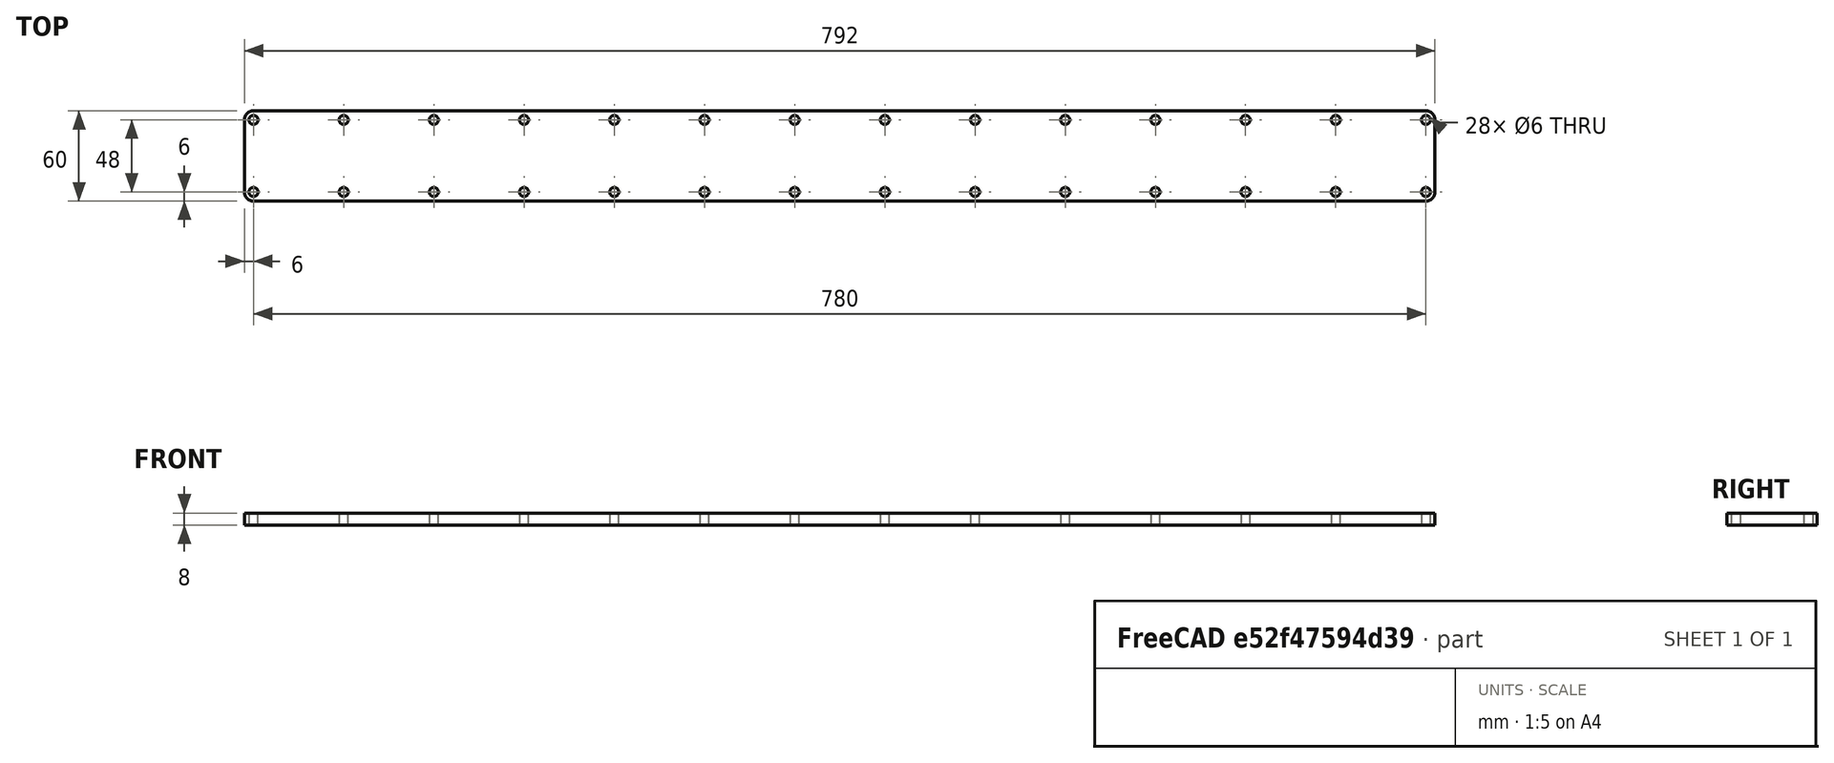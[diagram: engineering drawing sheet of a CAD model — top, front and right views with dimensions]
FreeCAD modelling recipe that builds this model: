
FCSTD DOCUMENT  (FreeCAD 0.19R24366 (Git))
Label: Tapped plate for slider rail mounting
License: All rights reserved
LicenseURL: http://en.wikipedia.org/wiki/All_rights_reserved
objects: Sketcher::SketchObject×1, PartDesign::Pad×1, PartDesign::Body×1
note: 4 computed .brp shape members not serialized (recipe doc carries the construction recipe); baked Part::Feature solids carry a one-line shape summary decoded from their .brp

FEATURE [Sketcher::SketchObject] Sketch  label="Plate sketch"
  FullyConstrained = true
  MapMode = 5
  Support = -> [XY_Plane]
  sketch-geometry (121):
    g0: LineSegment StartX=0 StartY=-1e-16 StartZ=0 EndX=0 EndY=24 EndZ=0
    g1: LineSegment StartX=0 StartY=-1e-16 StartZ=0 EndX=0 EndY=-24 EndZ=0
    g2: LineSegment StartX=0 StartY=24 StartZ=0 EndX=6 EndY=24 EndZ=0
    g3: LineSegment StartX=0 StartY=-24 StartZ=0 EndX=6 EndY=-24 EndZ=0
    g4: Circle CenterX=6 CenterY=-24 CenterZ=0 NormalX=0 NormalY=0 NormalZ=1 AngleXU=0 Radius=3
    g5: Circle CenterX=6 CenterY=24 CenterZ=0 NormalX=0 NormalY=0 NormalZ=1 AngleXU=0 Radius=3
    g6: ArcOfCircle CenterX=6 CenterY=24 CenterZ=0 NormalX=0 NormalY=0 NormalZ=1 AngleXU=0 Radius=6 StartAngle=1.5708 EndAngle=3.14159
    g7: ArcOfCircle CenterX=6 CenterY=-24 CenterZ=0 NormalX=0 NormalY=0 NormalZ=1 AngleXU=0 Radius=6 StartAngle=3.14159 EndAngle=4.71239
    g8: LineSegment StartX=786 StartY=-30 StartZ=0 EndX=6 EndY=-30 EndZ=0
    g9: LineSegment StartX=6 StartY=30 StartZ=0 EndX=786 EndY=30 EndZ=0
    g10: Circle CenterX=66 CenterY=24 CenterZ=0 NormalX=0 NormalY=0 NormalZ=1 AngleXU=0 Radius=3
    g11: LineSegment StartX=6 StartY=24 StartZ=0 EndX=66 EndY=24 EndZ=0
    g12: Circle CenterX=126 CenterY=24 CenterZ=0 NormalX=0 NormalY=0 NormalZ=1 AngleXU=0 Radius=3
    g13: LineSegment StartX=66 StartY=24 StartZ=0 EndX=126 EndY=24 EndZ=0
    g14: Circle CenterX=186 CenterY=24 CenterZ=0 NormalX=0 NormalY=0 NormalZ=1 AngleXU=0 Radius=3
    g15: LineSegment StartX=126 StartY=24 StartZ=0 EndX=186 EndY=24 EndZ=0
    g16: Circle CenterX=246 CenterY=24 CenterZ=0 NormalX=0 NormalY=0 NormalZ=1 AngleXU=0 Radius=3
    g17: LineSegment StartX=186 StartY=24 StartZ=0 EndX=246 EndY=24 EndZ=0
    g18: Circle CenterX=306 CenterY=24 CenterZ=0 NormalX=0 NormalY=0 NormalZ=1 AngleXU=0 Radius=3
    g19: LineSegment StartX=246 StartY=24 StartZ=0 EndX=306 EndY=24 EndZ=0
    g20: Circle CenterX=366 CenterY=24 CenterZ=0 NormalX=0 NormalY=0 NormalZ=1 AngleXU=0 Radius=3
    g21: LineSegment StartX=306 StartY=24 StartZ=0 EndX=366 EndY=24 EndZ=0
    g22: Circle CenterX=426 CenterY=24 CenterZ=0 NormalX=0 NormalY=0 NormalZ=1 AngleXU=0 Radius=3
    g23: LineSegment StartX=366 StartY=24 StartZ=0 EndX=426 EndY=24 EndZ=0
    g24: Circle CenterX=486 CenterY=24 CenterZ=0 NormalX=0 NormalY=0 NormalZ=1 AngleXU=0 Radius=3
    g25: LineSegment StartX=426 StartY=24 StartZ=0 EndX=486 EndY=24 EndZ=0
    g26: Circle CenterX=546 CenterY=24 CenterZ=0 NormalX=0 NormalY=0 NormalZ=1 AngleXU=0 Radius=3
    g27: LineSegment StartX=486 StartY=24 StartZ=0 EndX=546 EndY=24 EndZ=0
    g28: Circle CenterX=606 CenterY=24 CenterZ=0 NormalX=0 NormalY=0 NormalZ=1 AngleXU=0 Radius=3
    g29: LineSegment StartX=546 StartY=24 StartZ=0 EndX=606 EndY=24 EndZ=0
    g30: Circle CenterX=666 CenterY=24 CenterZ=0 NormalX=0 NormalY=0 NormalZ=1 AngleXU=0 Radius=3
    g31: LineSegment StartX=606 StartY=24 StartZ=0 EndX=666 EndY=24 EndZ=0
    g32: Circle CenterX=726 CenterY=24 CenterZ=0 NormalX=0 NormalY=0 NormalZ=1 AngleXU=0 Radius=3
    g33: LineSegment StartX=666 StartY=24 StartZ=0 EndX=726 EndY=24 EndZ=0
    g34: Circle CenterX=786 CenterY=24 CenterZ=0 NormalX=0 NormalY=0 NormalZ=1 AngleXU=0 Radius=3
    g35: LineSegment StartX=726 StartY=24 StartZ=0 EndX=786 EndY=24 EndZ=0
    g36: Circle CenterX=66 CenterY=-24 CenterZ=0 NormalX=0 NormalY=0 NormalZ=1 AngleXU=0 Radius=3
    g37: LineSegment StartX=6 StartY=-24 StartZ=0 EndX=66 EndY=-24 EndZ=0
    g38: Circle CenterX=126 CenterY=-24 CenterZ=0 NormalX=0 NormalY=0 NormalZ=1 AngleXU=0 Radius=3
    g39: LineSegment StartX=66 StartY=-24 StartZ=0 EndX=126 EndY=-24 EndZ=0
    g40: Circle CenterX=186 CenterY=-24 CenterZ=0 NormalX=0 NormalY=0 NormalZ=1 AngleXU=0 Radius=3
    g41: LineSegment StartX=126 StartY=-24 StartZ=0 EndX=186 EndY=-24 EndZ=0
    g42: Circle CenterX=246 CenterY=-24 CenterZ=0 NormalX=0 NormalY=0 NormalZ=1 AngleXU=0 Radius=3
    g43: LineSegment StartX=186 StartY=-24 StartZ=0 EndX=246 EndY=-24 EndZ=0
    g44: Circle CenterX=306 CenterY=-24 CenterZ=0 NormalX=0 NormalY=0 NormalZ=1 AngleXU=0 Radius=3
    g45: LineSegment StartX=246 StartY=-24 StartZ=0 EndX=306 EndY=-24 EndZ=0
    g46: Circle CenterX=366 CenterY=-24 CenterZ=0 NormalX=0 NormalY=0 NormalZ=1 AngleXU=0 Radius=3
    g47: LineSegment StartX=306 StartY=-24 StartZ=0 EndX=366 EndY=-24 EndZ=0
    g48: Circle CenterX=426 CenterY=-24 CenterZ=0 NormalX=0 NormalY=0 NormalZ=1 AngleXU=0 Radius=3
    g49: LineSegment StartX=366 StartY=-24 StartZ=0 EndX=426 EndY=-24 EndZ=0
    g50: Circle CenterX=486 CenterY=-24 CenterZ=0 NormalX=0 NormalY=0 NormalZ=1 AngleXU=0 Radius=3
    g51: LineSegment StartX=426 StartY=-24 StartZ=0 EndX=486 EndY=-24 EndZ=0
    g52: Circle CenterX=546 CenterY=-24 CenterZ=0 NormalX=0 NormalY=0 NormalZ=1 AngleXU=0 Radius=3
    g53: LineSegment StartX=486 StartY=-24 StartZ=0 EndX=546 EndY=-24 EndZ=0
    g54: Circle CenterX=606 CenterY=-24 CenterZ=0 NormalX=0 NormalY=0 NormalZ=1 AngleXU=0 Radius=3
    g55: LineSegment StartX=546 StartY=-24 StartZ=0 EndX=606 EndY=-24 EndZ=0
    g56: Circle CenterX=666 CenterY=-24 CenterZ=0 NormalX=0 NormalY=0 NormalZ=1 AngleXU=0 Radius=3
    g57: LineSegment StartX=606 StartY=-24 StartZ=0 EndX=666 EndY=-24 EndZ=0
    g58: Circle CenterX=726 CenterY=-24 CenterZ=0 NormalX=0 NormalY=0 NormalZ=1 AngleXU=0 Radius=3
    g59: LineSegment StartX=666 StartY=-24 StartZ=0 EndX=726 EndY=-24 EndZ=0
    g60: Circle CenterX=786 CenterY=-24 CenterZ=0 NormalX=0 NormalY=0 NormalZ=1 AngleXU=0 Radius=3
    g61: LineSegment StartX=726 StartY=-24 StartZ=0 EndX=786 EndY=-24 EndZ=0
    g62: ArcOfCircle CenterX=786 CenterY=-24 CenterZ=0 NormalX=0 NormalY=0 NormalZ=1 AngleXU=0 Radius=6 StartAngle=4.71239 EndAngle=6.28319
    g63: ArcOfCircle CenterX=786 CenterY=24 CenterZ=0 NormalX=0 NormalY=0 NormalZ=1 AngleXU=0 Radius=6 StartAngle=1.62478e-06 EndAngle=1.5708
    g64: LineSegment StartX=792 StartY=24 StartZ=0 EndX=792 EndY=-24 EndZ=0
    g65: LineSegment StartX=3 StartY=24 StartZ=0 EndX=9 EndY=24 EndZ=0
    g66: LineSegment StartX=6 StartY=27 StartZ=0 EndX=6 EndY=21 EndZ=0
    g67: LineSegment StartX=66 StartY=27 StartZ=0 EndX=66 EndY=21 EndZ=0
    g68: LineSegment StartX=63 StartY=24 StartZ=0 EndX=69 EndY=24 EndZ=0
    g69: LineSegment StartX=126 StartY=27 StartZ=0 EndX=126 EndY=21 EndZ=0
    g70: LineSegment StartX=123 StartY=24 StartZ=0 EndX=129 EndY=24 EndZ=0
    g71: LineSegment StartX=186 StartY=27 StartZ=0 EndX=186 EndY=21 EndZ=0
    g72: LineSegment StartX=183 StartY=24 StartZ=0 EndX=189 EndY=24 EndZ=0
    g73: LineSegment StartX=246 StartY=27 StartZ=0 EndX=246 EndY=21 EndZ=0
    g74: LineSegment StartX=243 StartY=24 StartZ=0 EndX=249 EndY=24 EndZ=0
    g75: LineSegment StartX=306 StartY=27 StartZ=0 EndX=306 EndY=21 EndZ=0
    g76: LineSegment StartX=303 StartY=24 StartZ=0 EndX=309 EndY=24 EndZ=0
    g77: LineSegment StartX=366 StartY=27 StartZ=0 EndX=366 EndY=21 EndZ=0
    g78: LineSegment StartX=363 StartY=24 StartZ=0 EndX=369 EndY=24 EndZ=0
    g79: LineSegment StartX=426 StartY=27 StartZ=0 EndX=426 EndY=21 EndZ=0
    g80: LineSegment StartX=423 StartY=24 StartZ=0 EndX=429 EndY=24 EndZ=0
    g81: LineSegment StartX=486 StartY=27 StartZ=0 EndX=486 EndY=21 EndZ=0
    g82: LineSegment StartX=483 StartY=24 StartZ=0 EndX=489 EndY=24 EndZ=0
    g83: LineSegment StartX=546 StartY=27 StartZ=0 EndX=546 EndY=21 EndZ=0
    g84: LineSegment StartX=543 StartY=24 StartZ=0 EndX=549 EndY=24 EndZ=0
    g85: LineSegment StartX=606 StartY=27 StartZ=0 EndX=606 EndY=21 EndZ=0
    g86: LineSegment StartX=603 StartY=24 StartZ=0 EndX=609 EndY=24 EndZ=0
    g87: LineSegment StartX=666 StartY=27 StartZ=0 EndX=666 EndY=21 EndZ=0
    g88: LineSegment StartX=663 StartY=24 StartZ=0 EndX=669 EndY=24 EndZ=0
    g89: LineSegment StartX=726 StartY=27 StartZ=0 EndX=726 EndY=21 EndZ=0
    g90: LineSegment StartX=723 StartY=24 StartZ=0 EndX=729 EndY=24 EndZ=0
    g91: LineSegment StartX=786 StartY=27 StartZ=0 EndX=786 EndY=21 EndZ=0
    g92: LineSegment StartX=783 StartY=24 StartZ=0 EndX=789 EndY=24 EndZ=0
    g93: LineSegment StartX=6 StartY=-21 StartZ=0 EndX=6 EndY=-27 EndZ=0
    g94: LineSegment StartX=3 StartY=-24 StartZ=0 EndX=9 EndY=-24 EndZ=0
    g95: LineSegment StartX=63 StartY=-24 StartZ=0 EndX=69 EndY=-24 EndZ=0
    g96: LineSegment StartX=66 StartY=-21 StartZ=0 EndX=66 EndY=-27 EndZ=0
    g97: LineSegment StartX=126 StartY=-21 StartZ=0 EndX=126 EndY=-27 EndZ=0
    g98: LineSegment StartX=123 StartY=-24 StartZ=0 EndX=129 EndY=-24 EndZ=0
    g99: LineSegment StartX=186 StartY=-21 StartZ=0 EndX=186 EndY=-27 EndZ=0
    g100: LineSegment StartX=183 StartY=-24 StartZ=0 EndX=189 EndY=-24 EndZ=0
    g101: LineSegment StartX=246 StartY=-21 StartZ=0 EndX=246 EndY=-27 EndZ=0
    g102: LineSegment StartX=243 StartY=-24 StartZ=0 EndX=249 EndY=-24 EndZ=0
    g103: LineSegment StartX=306 StartY=-21 StartZ=0 EndX=306 EndY=-27 EndZ=0
    g104: LineSegment StartX=303 StartY=-24 StartZ=0 EndX=309 EndY=-24 EndZ=0
    g105: LineSegment StartX=366 StartY=-21 StartZ=0 EndX=366 EndY=-27 EndZ=0
    g106: LineSegment StartX=363 StartY=-24 StartZ=0 EndX=369 EndY=-24 EndZ=0
    g107: LineSegment StartX=426 StartY=-21 StartZ=0 EndX=426 EndY=-27 EndZ=0
    g108: LineSegment StartX=423 StartY=-24 StartZ=0 EndX=429 EndY=-24 EndZ=0
    g109: LineSegment StartX=486 StartY=-21 StartZ=0 EndX=486 EndY=-27 EndZ=0
    g110: LineSegment StartX=483 StartY=-24 StartZ=0 EndX=489 EndY=-24 EndZ=0
    g111: LineSegment StartX=546 StartY=-21 StartZ=0 EndX=546 EndY=-27 EndZ=0
    g112: LineSegment StartX=543 StartY=-24 StartZ=0 EndX=549 EndY=-24 EndZ=0
    g113: LineSegment StartX=606 StartY=-21 StartZ=0 EndX=606 EndY=-27 EndZ=0
    g114: LineSegment StartX=603 StartY=-24 StartZ=0 EndX=609 EndY=-24 EndZ=0
    g115: LineSegment StartX=666 StartY=-21 StartZ=0 EndX=666 EndY=-27 EndZ=0
    g116: LineSegment StartX=663 StartY=-24 StartZ=0 EndX=669 EndY=-24 EndZ=0
    g117: LineSegment StartX=726 StartY=-21 StartZ=0 EndX=726 EndY=-27 EndZ=0
    g118: LineSegment StartX=723 StartY=-24 StartZ=0 EndX=729 EndY=-24 EndZ=0
    g119: LineSegment StartX=786 StartY=-21 StartZ=0 EndX=786 EndY=-27 EndZ=0
    g120: LineSegment StartX=783 StartY=-24 StartZ=0 EndX=789 EndY=-24 EndZ=0
  constraints (387):
    c: Coincident(g0,g-1)
    c: PointOnObject(g0,g-2)
    c: Coincident(g1,g0)
    c: PointOnObject(g1,g-2)
    c: DistanceY(g1,g0) = 48  'W from slider'
    c: Equal(g1,g0)
    c: Coincident(g2,g0)
    c: Horizontal(g2)
    c: Coincident(g3,g1)
    c: Horizontal(g3)
    c: Equal(g3,g2)
    c: DistanceX(g3,g3) = 6  'E from rails'
    c: Coincident(g4,g3)
    c: Coincident(g5,g2)
    c: Radius(g5) = 3  'M5 hole to drill out then tap'
    c: Coincident(g6,g5)
    c: Coincident(g7,g4)
    c: Horizontal(g8)
    c: Horizontal(g9)
    c: Tangent(g6,g9) = 1.5708
    c: Coincident(g6,g0)
    c: Coincident(g7,g1)
    c: Tangent(g7,g8) = 1.5708
    c: Equal(g5,g10) = 2.1
    c: Coincident(g5,g11)
    c: Coincident(g10,g11)
    c: Distance(g11) = 60  'P from rail'
    c: Angle(g11) = 0
    c: Equal(g5,g12) = 2.1
    c: Coincident(g10,g13)
    c: Coincident(g12,g13)
    c: Equal(g11,g13)
    c: Parallel(g13,g11)
    c: Equal(g5,g14) = 2.1
    c: Coincident(g12,g15)
    c: Coincident(g14,g15)
    c: Equal(g11,g15)
    c: Parallel(g15,g11)
    c: Equal(g5,g16) = 2.1
    c: Coincident(g14,g17)
    c: Coincident(g16,g17)
    c: Equal(g11,g17)
    c: Parallel(g17,g11)
    c: Equal(g5,g18) = 2.1
    c: Coincident(g16,g19)
    c: Coincident(g18,g19)
    c: Equal(g11,g19)
    c: Parallel(g19,g11)
    c: Equal(g5,g20) = 2.1
    c: Coincident(g18,g21)
    c: Coincident(g20,g21)
    c: Equal(g11,g21)
    c: Parallel(g21,g11)
    c: Equal(g5,g22) = 2.1
    c: Coincident(g20,g23)
    c: Coincident(g22,g23)
    c: Equal(g11,g23)
    c: Parallel(g23,g11)
    c: Equal(g5,g24) = 2.1
    c: Coincident(g22,g25)
    c: Coincident(g24,g25)
    c: Equal(g11,g25)
    c: Parallel(g25,g11)
    c: Equal(g5,g26) = 2.1
    c: Coincident(g24,g27)
    c: Coincident(g26,g27)
    c: Equal(g11,g27)
    c: Parallel(g27,g11)
    c: Equal(g5,g28) = 2.1
    c: Coincident(g26,g29)
    c: Coincident(g28,g29)
    c: Equal(g11,g29)
    c: Parallel(g29,g11)
    c: Equal(g5,g30) = 2.1
    c: Coincident(g28,g31)
    c: Coincident(g30,g31)
    c: Equal(g11,g31)
    c: Parallel(g31,g11)
    c: Equal(g5,g32) = 2.1
    c: Coincident(g30,g33)
    c: Coincident(g32,g33)
    c: Equal(g11,g33)
    c: Parallel(g33,g11)
    c: Equal(g5,g34) = 2.1
    c: Coincident(g32,g35)
    c: Coincident(g34,g35)
    c: Equal(g11,g35)
    c: Parallel(g35,g11)
    c: Equal(g4,g36) = 2.1
    c: Coincident(g4,g37)
    c: Coincident(g36,g37)
    c: Angle(g37) = 0
    c: Equal(g4,g38) = 2.1
    c: Coincident(g36,g39)
    c: Coincident(g38,g39)
    c: Equal(g37,g39)
    c: Parallel(g39,g37)
    c: Equal(g4,g40) = 2.1
    c: Coincident(g38,g41)
    c: Coincident(g40,g41)
    c: Equal(g37,g41)
    c: Parallel(g41,g37)
    c: Equal(g4,g42) = 2.1
    c: Coincident(g40,g43)
    c: Coincident(g42,g43)
    c: Equal(g37,g43)
    c: Parallel(g43,g37)
    c: Equal(g4,g44) = 2.1
    c: Coincident(g42,g45)
    c: Coincident(g44,g45)
    c: Equal(g37,g45)
    c: Parallel(g45,g37)
    c: Equal(g4,g46) = 2.1
    c: Coincident(g44,g47)
    c: Coincident(g46,g47)
    c: Equal(g37,g47)
    c: Parallel(g47,g37)
    c: Equal(g4,g48) = 2.1
    c: Coincident(g46,g49)
    c: Coincident(g48,g49)
    c: Equal(g37,g49)
    c: Parallel(g49,g37)
    c: Equal(g4,g50) = 2.1
    c: Coincident(g48,g51)
    c: Coincident(g50,g51)
    c: Equal(g37,g51)
    c: Parallel(g51,g37)
    c: Equal(g4,g52) = 2.1
    c: Coincident(g50,g53)
    c: Coincident(g52,g53)
    c: Equal(g37,g53)
    c: Parallel(g53,g37)
    c: Equal(g4,g54) = 2.1
    c: Coincident(g52,g55)
    c: Coincident(g54,g55)
    c: Equal(g37,g55)
    c: Parallel(g55,g37)
    c: Equal(g4,g56) = 2.1
    c: Coincident(g54,g57)
    c: Coincident(g56,g57)
    c: Equal(g37,g57)
    c: Parallel(g57,g37)
    c: Equal(g4,g58) = 2.1
    c: Coincident(g56,g59)
    c: Coincident(g58,g59)
    c: Equal(g37,g59)
    c: Parallel(g59,g37)
    c: Equal(g4,g60) = 2.1
    c: Coincident(g58,g61)
    c: Coincident(g60,g61)
    c: Equal(g37,g61)
    c: Parallel(g61,g37)
    c: Coincident(g62,g60)
    c: Coincident(g63,g34)
    c: Vertical(g64)
    c: Coincident(g63,g64)
    c: Tangent(g63,g9) = 1.5708
    c: Tangent(g62,g64) = 1.5708
    c: Tangent(g62,g8) = 1.5708
    c: Equal(g37,g11)
    c: Equal(g5,g4)
    c: DistanceX(g60,g62) = 6
    c: DistanceX(g1,g62) = 792
    c: PointOnObject(g65,g5)
    c: PointOnObject(g65,g5)
    c: Horizontal(g65)
    c: PointOnObject(g5,g65)
    c: PointOnObject(g66,g5)
    c: PointOnObject(g66,g5)
    c: Vertical(g66)
    c: PointOnObject(g5,g66)
    c: PointOnObject(g67,g10)
    c: PointOnObject(g67,g10)
    c: Vertical(g67)
    c: PointOnObject(g68,g10)
    c: PointOnObject(g68,g10)
    c: Horizontal(g68)
    c: PointOnObject(g69,g12)
    c: PointOnObject(g69,g12)
    c: Vertical(g69)
    c: PointOnObject(g70,g12)
    c: PointOnObject(g70,g12)
    c: Horizontal(g70)
    c: PointOnObject(g71,g14)
    c: PointOnObject(g71,g14)
    c: Vertical(g71)
    c: PointOnObject(g72,g14)
    c: PointOnObject(g72,g14)
    c: Horizontal(g72)
    c: PointOnObject(g73,g16)
    c: PointOnObject(g73,g16)
    c: Vertical(g73)
    c: PointOnObject(g74,g16)
    c: Horizontal(g74)
    c: PointOnObject(g75,g18)
    c: PointOnObject(g75,g18)
    c: PointOnObject(g76,g18)
    c: PointOnObject(g76,g18)
    c: Horizontal(g76)
    c: PointOnObject(g77,g20)
    c: PointOnObject(g77,g20)
    c: Vertical(g77)
    c: PointOnObject(g78,g20)
    c: PointOnObject(g78,g20)
    c: Horizontal(g78)
    c: PointOnObject(g79,g22)
    c: PointOnObject(g79,g22)
    c: Vertical(g79)
    c: PointOnObject(g80,g22)
    c: PointOnObject(g80,g22)
    c: Horizontal(g80)
    c: PointOnObject(g81,g24)
    c: PointOnObject(g81,g24)
    c: Vertical(g81)
    c: PointOnObject(g82,g24)
    c: PointOnObject(g82,g24)
    c: Horizontal(g82)
    c: PointOnObject(g83,g26)
    c: PointOnObject(g83,g26)
    c: Vertical(g83)
    c: PointOnObject(g84,g26)
    c: PointOnObject(g84,g26)
    c: Horizontal(g84)
    c: PointOnObject(g85,g28)
    c: PointOnObject(g85,g28)
    c: Vertical(g85)
    c: PointOnObject(g86,g28)
    c: PointOnObject(g86,g28)
    c: Horizontal(g86)
    c: PointOnObject(g87,g30)
    c: PointOnObject(g87,g30)
    c: Vertical(g87)
    c: PointOnObject(g88,g30)
    c: PointOnObject(g88,g30)
    c: Horizontal(g88)
    c: PointOnObject(g89,g32)
    c: PointOnObject(g89,g32)
    c: Vertical(g89)
    c: PointOnObject(g90,g32)
    c: PointOnObject(g90,g32)
    c: Horizontal(g90)
    c: PointOnObject(g91,g34)
    c: PointOnObject(g91,g34)
    c: PointOnObject(g92,g34)
    c: PointOnObject(g92,g34)
    c: Horizontal(g92)
    c: Vertical(g91)
    c: PointOnObject(g34,g92)
    c: PointOnObject(g34,g91)
    c: PointOnObject(g32,g90)
    c: PointOnObject(g32,g89)
    c: PointOnObject(g30,g88)
    c: PointOnObject(g30,g87)
    c: PointOnObject(g28,g86)
    c: PointOnObject(g28,g85)
    c: PointOnObject(g26,g84)
    c: PointOnObject(g26,g83)
    c: PointOnObject(g24,g82)
    c: PointOnObject(g24,g81)
    c: PointOnObject(g22,g80)
    c: PointOnObject(g22,g79)
    c: PointOnObject(g20,g78)
    c: PointOnObject(g20,g77)
    c: Vertical(g75)
    c: PointOnObject(g18,g75)
    c: PointOnObject(g18,g76)
    c: PointOnObject(g16,g73)
    c: PointOnObject(g16,g74)
    c: PointOnObject(g74,g16)
    c: PointOnObject(g14,g72)
    c: PointOnObject(g14,g71)
    c: PointOnObject(g12,g69)
    c: PointOnObject(g12,g70)
    c: PointOnObject(g10,g68)
    c: PointOnObject(g10,g67)
    c: PointOnObject(g93,g4)
    c: PointOnObject(g93,g4)
    c: Vertical(g93)
    c: PointOnObject(g94,g4)
    c: PointOnObject(g94,g4)
    c: Horizontal(g94)
    c: PointOnObject(g95,g36)
    c: PointOnObject(g95,g36)
    c: Horizontal(g95)
    c: PointOnObject(g96,g36)
    c: PointOnObject(g96,g36)
    c: Vertical(g96)
    c: PointOnObject(g97,g38)
    c: PointOnObject(g97,g38)
    c: Vertical(g97)
    c: PointOnObject(g98,g38)
    c: PointOnObject(g98,g38)
    c: Horizontal(g98)
    c: PointOnObject(g99,g40)
    c: PointOnObject(g99,g40)
    c: Vertical(g99)
    c: PointOnObject(g100,g40)
    c: PointOnObject(g100,g40)
    c: Horizontal(g100)
    c: PointOnObject(g101,g42)
    c: PointOnObject(g101,g42)
    c: Vertical(g101)
    c: PointOnObject(g102,g42)
    c: PointOnObject(g102,g42)
    c: Horizontal(g102)
    c: PointOnObject(g103,g44)
    c: PointOnObject(g103,g44)
    c: PointOnObject(g104,g44)
    c: PointOnObject(g104,g44)
    c: Horizontal(g104)
    c: PointOnObject(g105,g46)
    c: PointOnObject(g105,g46)
    c: Vertical(g105)
    c: PointOnObject(g106,g46)
    c: PointOnObject(g106,g46)
    c: Horizontal(g106)
    c: PointOnObject(g107,g48)
    c: PointOnObject(g107,g48)
    c: Vertical(g107)
    c: PointOnObject(g108,g48)
    c: PointOnObject(g108,g48)
    c: Horizontal(g108)
    c: PointOnObject(g109,g50)
    c: PointOnObject(g109,g50)
    c: Vertical(g109)
    c: PointOnObject(g110,g50)
    c: PointOnObject(g110,g50)
    c: Horizontal(g110)
    c: PointOnObject(g111,g52)
    c: PointOnObject(g111,g52)
    c: PointOnObject(g112,g52)
    c: PointOnObject(g112,g52)
    c: Horizontal(g112)
    c: PointOnObject(g113,g54)
    c: PointOnObject(g113,g54)
    c: Vertical(g113)
    c: PointOnObject(g114,g54)
    c: PointOnObject(g114,g54)
    c: Horizontal(g114)
    c: PointOnObject(g115,g56)
    c: PointOnObject(g115,g56)
    c: Vertical(g115)
    c: PointOnObject(g116,g56)
    c: PointOnObject(g116,g56)
    c: Horizontal(g116)
    c: PointOnObject(g117,g58)
    c: PointOnObject(g117,g58)
    c: Vertical(g117)
    c: PointOnObject(g118,g58)
    c: PointOnObject(g118,g58)
    c: Horizontal(g118)
    c: PointOnObject(g119,g60)
    c: PointOnObject(g119,g60)
    c: Vertical(g119)
    c: PointOnObject(g120,g60)
    c: PointOnObject(g120,g60)
    c: Horizontal(g120)
    c: PointOnObject(g60,g119)
    c: PointOnObject(g60,g120)
    c: PointOnObject(g58,g117)
    c: PointOnObject(g58,g118)
    c: PointOnObject(g56,g116)
    c: PointOnObject(g56,g115)
    c: PointOnObject(g54,g113)
    c: PointOnObject(g54,g114)
    c: PointOnObject(g52,g112)
    c: Vertical(g111)
    c: PointOnObject(g52,g111)
    c: PointOnObject(g50,g110)
    c: PointOnObject(g50,g109)
    c: PointOnObject(g48,g108)
    c: PointOnObject(g48,g107)
    c: PointOnObject(g46,g106)
    c: PointOnObject(g46,g105)
    c: PointOnObject(g44,g104)
    c: Vertical(g103)
    c: PointOnObject(g44,g103)
    c: PointOnObject(g42,g101)
    c: PointOnObject(g42,g102)
    c: PointOnObject(g40,g100)
    c: PointOnObject(g40,g99)
    c: PointOnObject(g38,g98)
    c: PointOnObject(g38,g97)
    c: PointOnObject(g36,g95)
    c: PointOnObject(g36,g96)
    c: PointOnObject(g4,g93)
    c: PointOnObject(g4,g94)
FEATURE [PartDesign::Pad] Pad  label="Plate thickness M5 tapped holes"
  Direction = (1,1,1)
  Length = 8
  Length2 = 100
  Profile = -> Sketch
  Type = 0
FEATURE [PartDesign::Body] Body
  Group = -> [Sketch,Pad]
  Origin = -> Origin
  Tip = -> Pad
